FCSTD DOCUMENT  (FreeCAD 1.0R39319 (Git))
Label: OctoForge-A
License: Creative Commons Attribution 4.0
LicenseURL: https://creativecommons.org/licenses/by/4.0/
objects: App::FeaturePython×6, App::LinkElement×4, App::Link×3, App::DocumentObjectGroup×1, Assembly::JointGroup×1, Assembly::AssemblyObject×1
EXTERNAL_REF file=Frame/OCT-FRAME-A.FCStd obj=Assembly
EXTERNAL_REF file=Insulation/OCT-CHMBR-A.FCStd obj=Assembly
EXTERNAL_REF file=Electronics/OCT-HELEM-A.FCStd obj=Part

FEATURE [App::Link] Link  label="OCT-FRAME-A"
  LinkPlacement = pos=(-67.4025,-29.5359,22.5821) rot=(0,0,1;0rad)
  LinkedObject = -> <external Frame/OCT-FRAME-A.FCStd>#Assembly
  Placement = pos=(-67.4025,-29.5359,22.5821) rot=(0,0,1;0rad)
FEATURE [App::FeaturePython] GroundedJoint  # Assembly grounded joint (typed FeaturePython)
  ObjectToGround = -> Link
  Placement = pos=(-67.4025,-29.5359,22.5821) rot=(0,0,1;0rad)
FEATURE [App::Link] Link001  label="OCT-CHMBR-A"
  LinkPlacement = pos=(-67.4025,-29.5359,185.582) rot=(0,0,1;0rad)
  LinkedObject = -> <external Insulation/OCT-CHMBR-A.FCStd>#Assembly
  Placement = pos=(-67.4025,-29.5359,185.582) rot=(0,0,1;0rad)
FEATURE [App::FeaturePython] Joint  label="Fixed"  # Assembly joint (typed FeaturePython)
  Activated = true
  AngleMax = 0
  AngleMin = 0
  Detach1 = false
  Detach2 = false
  Distance = 0
  Distance2 = 0
  EnableAngleMax = false
  EnableAngleMin = false
  EnableLengthMax = false
  EnableLengthMin = false
  JointType = 0 (Fixed)
  LengthMax = 0
  LengthMin = 0
  Offset2 = pos=(0,0,0) rot=(0,0,1;3.14159rad)
  Placement1 = pos=(3.2e-15,111,0) rot=(-0.707107,0,0.707107;3.14159rad)
  Placement2 = pos=(-3.2e-15,0,0) rot=(0,-1,0;4.71239rad)
  Reference1 = -> Assembly [Link001.OCT_CHBRK_BA.Edge21,Link001.OCT_CHBRK_BA.Edge21]
  Reference2 = -> Assembly [Link.brace.Edge5,Link.brace.Edge5]
FEATURE [App::LinkElement] OCT_HELEM_A_i0
  LinkPlacement = pos=(-67.4025,-29.5359,374.582) rot=(0,0,1;0.785398rad)
  LinkedObject = -> <external Electronics/OCT-HELEM-A.FCStd>#Part
  Placement = pos=(-67.4025,-29.5359,374.582) rot=(0,0,1;0.785398rad)
  _LinkOwner = 55
FEATURE [App::LinkElement] OCT_HELEM_A_i1
  LinkPlacement = pos=(-67.4025,-29.5359,341.582) rot=(0,0,1;0.785398rad)
  LinkedObject = -> <external Electronics/OCT-HELEM-A.FCStd>#Part
  Placement = pos=(-67.4025,-29.5359,341.582) rot=(0,0,1;0.785398rad)
  _LinkOwner = 55
FEATURE [App::LinkElement] OCT_HELEM_A_i2
  LinkPlacement = pos=(-67.4025,-29.5359,308.582) rot=(0,0,1;0.785398rad)
  LinkedObject = -> <external Electronics/OCT-HELEM-A.FCStd>#Part
  Placement = pos=(-67.4025,-29.5359,308.582) rot=(0,0,1;0.785398rad)
  _LinkOwner = 55
FEATURE [App::LinkElement] OCT_HELEM_A_i3
  LinkPlacement = pos=(-67.4025,-29.5359,275.582) rot=(0,0,1;0.785398rad)
  LinkedObject = -> <external Electronics/OCT-HELEM-A.FCStd>#Part
  Placement = pos=(-67.4025,-29.5359,275.582) rot=(0,0,1;0.785398rad)
  _LinkOwner = 55
FEATURE [App::Link] OCT_HELEM_A  label="OCT-HELEM-A"
  ElementCount = 4
  ElementList = -> [OCT_HELEM_A_i0,OCT_HELEM_A_i1,OCT_HELEM_A_i2,OCT_HELEM_A_i3]
  LinkedObject = -> <external Electronics/OCT-HELEM-A.FCStd>#Part
FEATURE [App::DocumentObjectGroup] Group  label="Heating Elements"
  Group = -> [OCT_HELEM_A]
FEATURE [App::FeaturePython] Joint001  label="Fixed"  # Assembly joint (typed FeaturePython)
  Activated = true
  AngleMax = 0
  AngleMin = 0
  Detach1 = false
  Detach2 = false
  Distance = 0
  Distance2 = 0
  EnableAngleMax = false
  EnableAngleMin = false
  EnableLengthMax = false
  EnableLengthMin = false
  JointType = 0 (Fixed)
  LengthMax = 0
  LengthMin = 0
  Offset2 = pos=(0,0,0) rot=(0,0,-1;1.5708rad)
  Placement1 = pos=(-3.6e-15,-35,-7.1e-15) rot=(-1,0,0;4.71239rad)
  Placement2 = pos=(1.1e-14,35,189) rot=(0,-0.707107,-0.707107;3.14159rad)
  Reference1 = -> Assembly [OCT_HELEM_A.OCT_HELEM_A_i0.Link.Link_i1.Edge2,OCT_HELEM_A.OCT_HELEM_A_i0.Link.Link_i1.Edge2]
  Reference2 = -> Assembly [Link001.OCT_CHBRK_BA.Edge35,Link001.OCT_CHBRK_BA.Edge35]
FEATURE [App::FeaturePython] Joint002  label="Fixed"  # Assembly joint (typed FeaturePython)
  Activated = true
  AngleMax = 0
  AngleMin = 0
  Detach1 = false
  Detach2 = false
  Distance = 0
  Distance2 = 0
  EnableAngleMax = false
  EnableAngleMin = false
  EnableLengthMax = false
  EnableLengthMin = false
  JointType = 0 (Fixed)
  LengthMax = 0
  LengthMin = 0
  Offset2 = pos=(0,0,0) rot=(0,0,-1;1.5708rad)
  Placement1 = pos=(-3.6e-15,-35,-7.1e-15) rot=(-1,0,0;4.71239rad)
  Placement2 = pos=(7e-15,35,156) rot=(0,-0.707107,-0.707107;3.14159rad)
  Reference1 = -> Assembly [OCT_HELEM_A.OCT_HELEM_A_i1.Link.Link_i1.Edge2,OCT_HELEM_A.OCT_HELEM_A_i1.Link.Link_i1.Edge2]
  Reference2 = -> Assembly [Link001.OCT_CHBRK_BA.Edge49,Link001.OCT_CHBRK_BA.Edge49]
FEATURE [App::FeaturePython] Joint003  label="Fixed"  # Assembly joint (typed FeaturePython)
  Activated = true
  AngleMax = 0
  AngleMin = 0
  Detach1 = false
  Detach2 = false
  Distance = 0
  Distance2 = 0
  EnableAngleMax = false
  EnableAngleMin = false
  EnableLengthMax = false
  EnableLengthMin = false
  JointType = 0 (Fixed)
  LengthMax = 0
  LengthMin = 0
  Offset2 = pos=(0,0,0) rot=(0,0,-1;1.5708rad)
  Placement1 = pos=(-3.6e-15,-35,-7.1e-15) rot=(-1,0,0;4.71239rad)
  Placement2 = pos=(4e-15,35,123) rot=(0,-0.707107,-0.707107;3.14159rad)
  Reference1 = -> Assembly [OCT_HELEM_A.OCT_HELEM_A_i2.Link.Link_i1.Edge2,OCT_HELEM_A.OCT_HELEM_A_i2.Link.Link_i1.Edge2]
  Reference2 = -> Assembly [Link001.OCT_CHBRK_BA.Edge63,Link001.OCT_CHBRK_BA.Edge63]
FEATURE [App::FeaturePython] Joint004  label="Fixed"  # Assembly joint (typed FeaturePython)
  Activated = true
  AngleMax = 0
  AngleMin = 0
  Detach1 = false
  Detach2 = false
  Distance = 0
  Distance2 = 0
  EnableAngleMax = false
  EnableAngleMin = false
  EnableLengthMax = false
  EnableLengthMin = false
  JointType = 0 (Fixed)
  LengthMax = 0
  LengthMin = 0
  Offset2 = pos=(0,0,0) rot=(0,0,-1;1.5708rad)
  Placement1 = pos=(-3.6e-15,-35,-7.1e-15) rot=(-1,0,0;4.71239rad)
  Placement2 = pos=(0,35,90) rot=(0,-0.707107,-0.707107;3.14159rad)
  Reference1 = -> Assembly [OCT_HELEM_A.OCT_HELEM_A_i3.Link.Link_i1.Edge2,OCT_HELEM_A.OCT_HELEM_A_i3.Link.Link_i1.Edge2]
  Reference2 = -> Assembly [Link001.OCT_CHBRK_BA.Edge77,Link001.OCT_CHBRK_BA.Edge77]
FEATURE [Assembly::JointGroup] Joints
  Group = -> [GroundedJoint,Joint,Joint001,Joint002,Joint003,Joint004]
FEATURE [Assembly::AssemblyObject] Assembly  label="OctoForge"
  Group = -> [Joints,Link,GroundedJoint,Link001,Joint,Group,OCT_HELEM_A,Joint001,Joint002,Joint003,Joint004]
  Origin = -> Origin
  Type = Assembly

RESOLVED EXTERNAL PARTS (link-assembly join: the EXTERNAL_REF files above that resolve inside this repo's crawl, each included once):
---- part Electronics/OCT-HELEM-A.FCStd = doc fcstd_b4418c379665 ----
FCSTD DOCUMENT  (FreeCAD 1.0R39319 (Git))
Label: OCT-HELEM-A
License: Creative Commons Attribution 4.0
LicenseURL: https://creativecommons.org/licenses/by/4.0/
objects: Sketcher::SketchObject×9, Part::FeaturePython×9, PartDesign::Plane×3, PartDesign::SubShapeBinder×3, PartDesign::Line×2, PartDesign::Body×2, App::Part×2, App::LinkElement×2, App::VarSet×1, PartDesign::Point×1, PartDesign::AdditivePipe×1, PartDesign::Pad×1, App::Link×1, App::DocumentObjectGroup×1
note: 44 computed .brp shape members not serialized (recipe doc carries the construction recipe); baked Part::Feature solids carry a one-line shape summary decoded from their .brp

FEATURE [App::VarSet] VarSet  label="dims"
  arcAngle = 300
  barLength = 86
  brickThickness = 76
  chamberDiameter = 70
  coilDiameter = 6.02
  dTerminal = 4
  lWire = 866.98
  loopDiameter = 83
  pitch = 4.89634
  wireDiameter = 1.02
  expr: barLength = brickThickness + 10 mm
  expr: pitch = pi * coilDiameter * tan(asin(0.5 * loopDiameter * arcAngle * pi / (180 * lWire * 1 deg)))
FEATURE [Sketcher::SketchObject] Sketch006  label="coil path"
  ArcFitTolerance = 1e-06
  AttachmentSupport = -> [XY_Plane002]
  FullyConstrained = true
  MakeInternals = false
  MapMode = 5
  expr: Constraints[1] = <<dims>>.arcAngle
  expr: Constraints[3] = <<dims>>.loopDiameter / 2
  sketch-geometry (5):
    g0: ArcOfCircle CenterX=0 CenterY=0 CenterZ=0 NormalX=0 NormalY=0 NormalZ=1 AngleXU=0 Radius=41.5 StartAngle=4.84329 EndAngle=10.0793
    g1: LineSegment [constr] StartX=0 StartY=0 StartZ=0 EndX=-15.8814 EndY=-38.341 EndZ=0
    g2: LineSegment [constr] StartX=-32.9242 StartY=-25.2636 StartZ=0 EndX=-15.8814 EndY=-38.341 EndZ=0
    g3: LineSegment [constr] StartX=5.41684 StartY=-41.145 StartZ=0 EndX=-15.8814 EndY=-38.341 EndZ=0
    g4: LineSegment [constr] StartX=0 StartY=0 StartZ=0 EndX=-32.9242 EndY=-25.2636 EndZ=0
  constraints (14):
    c: Coincident(g0,g-1)
    c: Angle(g0) = 5.23599
    c: Coincident(g1,g0)
    c: Radius(g0) = 41.5
    c: PointOnObject(g1,g0)
    c: Coincident(g2,g0)
    c: Coincident(g2,g1)
    c: Coincident(g3,g0)
    c: Coincident(g3,g1)
    c: Equal(g2,g3)
    c: Coincident(g4,g0)
    c: Coincident(g4,g0)
    c: Angle(g-2,g4) = 2.22529
    c: Angle(g-2,g1) = 2.74889
FEATURE [PartDesign::Plane] DatumPlane  label="coil start right"
  AttachmentOffset = pos=(0,0,0) rot=(0,1,0;0.1309rad)
  AttachmentSupport = -> [YZ_Plane003]
  Length = 114.074
  MapMode = 5
  Placement = pos=(0,0,0) rot=(0.527011,0.600941,0.600941;2.17155rad)
  ResizeMode = 0
  Width = 64.1376
  expr: .AttachmentOffset.Rotation.Pitch = -22.5 + (360 - <<dims>>.arcAngle / deg) / 2
FEATURE [Part::FeaturePython] PathHelix  # WARN: FeaturePython — macro-defined, semantics opaque (R4)
  Count = 44.3787
  ExtraHalf = false
  Join = true
  Pitch = 4.89634
  Radius = 3.01
  Resolution = 4
  Reverse = true
  Rotation = 180
  Spine = -> Sketch006
  expr: Pitch = <<dims>>.pitch
  expr: Radius = <<dims>>.coilDiameter / 2
FEATURE [PartDesign::SubShapeBinder] Binder  label="loop binder"
  BindCopyOnChange = 0
  BindMode = 0
  ClaimChildren = false
  Context = -> Part [Part001.Body001.Binder.]
  Fuse = false
  MakeFace = true
  OffsetFill = false
  OffsetIntersection = false
  OffsetJoinType = 0
  OffsetOpenResult = false
  PartialLoad = false
  Relative = true
  Support = -> [Sketch006]
  _Version = 2
FEATURE [Sketcher::SketchObject] Sketch  label="terminal loop right"
  ArcFitTolerance = 1e-06
  AttachmentOffset = pos=(0,0,41.5) rot=(0,0,1;0rad)
  AttachmentSupport = -> [XZ_Plane003]
  FullyConstrained = true
  MakeInternals = false
  MapMode = 5
  Placement = pos=(0,-41.5,9.2e-15) rot=(1,0,0;1.5708rad)
  expr: .AttachmentOffset.Base.z = <<dims>>.loopDiameter / 2
  expr: Constraints[3] = (<<dims>>.dTerminal + <<dims>>.wireDiameter) / 2
  sketch-geometry (2):
    g0: ArcOfCircle CenterX=0 CenterY=0 CenterZ=0 NormalX=0 NormalY=0 NormalZ=1 AngleXU=0 Radius=2.51 StartAngle=0.288902 EndAngle=5.78669
    g1: ArcOfCircle CenterX=3.36454 CenterY=1 CenterZ=0 NormalX=0 NormalY=0 NormalZ=1 AngleXU=0 Radius=1 StartAngle=3.4305 EndAngle=4.71239
  constraints (6):
    c: Coincident(g0,g-1)
    c: Tangent(g0,g1) = 1.5708
    c: Tangent(g1,g-1) = -1.5708
    c: Radius(g0) = 2.51
    c: Radius(g1) = 1
    c: Angle(g0) = 5.49779
FEATURE [Sketcher::SketchObject] Sketch007  label="xy transition right"
  ArcFitTolerance = 1e-06
  AttachmentSupport = -> [XY_Plane003]
  ExternalGeometry = -> [Sketch,Binder]
  FullyConstrained = true
  MakeInternals = false
  MapMode = 5
  sketch-geometry (3):
    g0: ArcOfCircle CenterX=3.36454 CenterY=-40.4973 CenterZ=0 NormalX=0 NormalY=0 NormalZ=1 AngleXU=0 Radius=1.00271 StartAngle=4.71239 EndAngle=5.33537
    g1: ArcOfCircle CenterX=4.53463 CenterY=-42.126 CenterZ=0 NormalX=0 NormalY=0 NormalZ=1 AngleXU=0 Radius=1.00271 StartAngle=0.1309 EndAngle=2.19378
    g2: LineSegment [constr] StartX=5.52876 StartY=-41.9951 StartZ=0 EndX=0 EndY=0 EndZ=0
  constraints (7):
    c: Tangent(g1,g0) = 1.5708
    c: Tangent(g2,g1) = -1.5708
    c: Coincident(g2,g-1)
    c: PointOnObject(g-4,g2)
    c: PointOnObject(g0,g-4)
    c: Tangent(g-3,g0) = -1.5708
    c: Equal(g1,g0)
FEATURE [PartDesign::SubShapeBinder] Binder001  label="coil binder"
  BindCopyOnChange = 0
  BindMode = 0
  ClaimChildren = false
  Context = -> Part [Part001.Body001.Binder001.]
  Fuse = false
  MakeFace = true
  OffsetFill = false
  OffsetIntersection = false
  OffsetJoinType = 0
  OffsetOpenResult = false
  PartialLoad = false
  Relative = true
  Support = -> [PathHelix]
  _Version = 2
FEATURE [Sketcher::SketchObject] Sketch008  label="coil transition right"
  ArcFitTolerance = 1e-06
  AttachmentSupport = -> [DatumPlane]
  ExternalGeometry = -> [Binder001,Sketch007]
  FullyConstrained = true
  MakeInternals = false
  MapMode = 5
  Placement = pos=(0,0,0) rot=(0.527011,0.600941,0.600941;2.17155rad)
  expr: Constraints[1] = <<dims>>.loopDiameter / 2
  expr: Constraints[2] = <<dims>>.coilDiameter
  sketch-geometry (3):
    g0: Circle [constr] CenterX=-41.5 CenterY=0 CenterZ=0 NormalX=0 NormalY=0 NormalZ=1 AngleXU=0 Radius=3.01
    g1: ArcOfCircle CenterX=-42.3575 CenterY=1.38287 CenterZ=0 NormalX=0 NormalY=0 NormalZ=1 AngleXU=0 Radius=1.38287 StartAngle=2.12583 EndAngle=4.71238
    g2: ArcOfCircle CenterX=-41.5 CenterY=0 CenterZ=0 NormalX=0 NormalY=0 NormalZ=1 AngleXU=0 Radius=3.01 StartAngle=1.5708 EndAngle=2.12583
  constraints (8):
    c: PointOnObject(g0,g-1)
    c: DistanceX(g0,g-1) = 41.5
    c: Diameter(g0) = 6.02
    c: Coincident(g1,g-4)
    c: Tangent(g1,g-1)
    c: Coincident(g2,g-3)
    c: Coincident(g2,g0)
    c: Tangent(g1,g2) = -1.5708
FEATURE [Sketcher::SketchObject] Sketch009  label="wire cross section"
  ArcFitTolerance = 1e-06
  AttachmentSupport = -> [YZ_Plane003]
  FullyConstrained = true
  MakeInternals = false
  MapMode = 5
  Placement = pos=(0,0,0) rot=(0.57735,0.57735,0.57735;2.0944rad)
  expr: Constraints[0] = <<dims>>.wireDiameter
  expr: Constraints[1] = <<dims>>.loopDiameter / 2
  expr: Constraints[2] = (<<dims>>.dTerminal + <<dims>>.wireDiameter) / 2
  sketch-geometry (1):
    g0: Circle CenterX=-41.5 CenterY=-2.51 CenterZ=0 NormalX=0 NormalY=0 NormalZ=1 AngleXU=0 Radius=0.51
  constraints (3):
    c: Diameter(g0) = 1.02
    c: DistanceX(g0,g-1) = 41.5
    c: DistanceY(g0,g-1) = 2.51
FEATURE [PartDesign::Line] DatumLine  label="terminal axis left"
  AttacherType = Attacher::AttachEngineLine
  AttachmentOffset = pos=(0,0,0) rot=(0,-1,0;0.785398rad)
  AttachmentSupport = -> [Y_Axis003]
  Length = 20
  MapMode = 29
  Placement = pos=(0,0,0) rot=(0.281085,0.678598,0.678598;2.59356rad)
  ResizeMode = 0
FEATURE [PartDesign::Plane] DatumPlane001  label="terminal left plane"
  AttachmentOffset = pos=(0,0,41.5) rot=(0,0,1;0rad)
  AttachmentSupport = -> [DatumLine]
  Length = 142.427
  MapMode = 7
  Placement = pos=(-29.3449,-29.3449,0) rot=(0.862856,-0.357407,-0.357407;1.71777rad)
  ResizeMode = 0
  Width = 65.9072
  expr: .AttachmentOffset.Base.z = <<dims>>.loopDiameter / 2
FEATURE [Sketcher::SketchObject] Sketch010  label="terminal loop left"
  ArcFitTolerance = 1e-06
  AttachmentSupport = -> [DatumPlane001]
  FullyConstrained = true
  MakeInternals = false
  MapMode = 5
  Placement = pos=(-29.3449,-29.3449,0) rot=(0.862856,-0.357407,-0.357407;1.71777rad)
  expr: Constraints[1] = (<<dims>>.dTerminal + <<dims>>.wireDiameter) / 2
  sketch-geometry (2):
    g0: ArcOfCircle CenterX=0 CenterY=0 CenterZ=0 NormalX=0 NormalY=0 NormalZ=1 AngleXU=0 Radius=2.51 StartAngle=3.63809 EndAngle=9.13588
    g1: ArcOfCircle CenterX=-3.36454 CenterY=1 CenterZ=0 NormalX=0 NormalY=0 NormalZ=1 AngleXU=0 Radius=1 StartAngle=4.71239 EndAngle=5.99428
  constraints (6):
    c: Coincident(g0,g-1)
    c: Radius(g0) = 2.51
    c: Radius(g1) = 1
    c: Tangent(g1,g0) = 1.5708
    c: Tangent(g1,g-1) = -1.5708
    c: Angle(g0) = 5.49779
FEATURE [PartDesign::Point] DatumPoint  label="coil start point left"
  AttacherType = Attacher::AttachEnginePoint
  AttachmentSupport = -> [Binder001]
  MapMode = 37
  Placement = pos=(-34.0198,-23.7677,3.01) rot=(0,0,1;0rad)
FEATURE [PartDesign::Plane] DatumPlane002  label="coil start plane left"
  AttachmentSupport = -> [Binder001,Z_Axis003]
  Length = 140.493
  MapMode = 13
  Placement = pos=(-11.3399,-7.92258,1.33667) rot=(0.913595,0.287528,0.287528;1.66104rad)
  ResizeMode = 0
  Width = 65.7925
FEATURE [Sketcher::SketchObject] Sketch011  label="xy transition left"
  ArcFitTolerance = 1e-06
  AttachmentSupport = -> [XY_Plane003]
  ExternalGeometry = -> [Sketch010,Binder001]
  FullyConstrained = true
  MakeInternals = false
  MapMode = 5
  expr: Constraints[4] = <<dims>>.loopDiameter / 2
  sketch-geometry (4):
    g0: ArcOfCircle CenterX=-24.9661 CenterY=-20.2079 CenterZ=0 NormalX=0 NormalY=0 NormalZ=1 AngleXU=0 Radius=9.55715 StartAngle=3.60279 EndAngle=3.92699
    g1: ArcOfCircle CenterX=-32.6292 CenterY=-24.0161 CenterZ=0 NormalX=0 NormalY=0 NormalZ=1 AngleXU=0 Radius=1 StartAngle=2.18061 EndAngle=3.60279
    g2: LineSegment [constr] StartX=-33.5247 StartY=-24.4611 StartZ=0 EndX=0 EndY=3.6e-15 EndZ=0
    g3: LineSegment [constr] StartX=-34.0198 StartY=-23.7677 StartZ=0 EndX=0 EndY=0 EndZ=0
  constraints (9):
    c: Tangent(g0,g-3) = -1.5708
    c: Tangent(g0,g1) = -1.5708
    c: Coincident(g2,g0)
    c: Coincident(g2,g-1)
    c: Distance(g2,g2) = 41.5
    c: Coincident(g3,g-4)
    c: Coincident(g3,g2)
    c: Tangent(g1,g3) = 1.5708
    c: Radius(g1) = 1
FEATURE [Sketcher::SketchObject] Sketch012  label="coil transition left"
  ArcFitTolerance = 1e-06
  AttachmentSupport = -> [DatumPlane002]
  ExternalGeometry = -> [Sketch011,DatumPoint]
  FullyConstrained = true
  MakeInternals = false
  MapMode = 5
  Placement = pos=(-11.3399,-7.92258,1.33667) rot=(0.913595,0.287528,0.287528;1.66104rad)
  sketch-geometry (3):
    g0: Circle [constr] CenterX=-27.6579 CenterY=-1.33667 CenterZ=0 NormalX=0 NormalY=0 NormalZ=1 AngleXU=0 Radius=3.01001
    g1: ArcOfCircle CenterX=-26.6689 CenterY=0.00586924 CenterZ=0 NormalX=0 NormalY=0 NormalZ=1 AngleXU=0 Radius=1.34254 StartAngle=4.71239 EndAngle=7.21908
    g2: ArcOfCircle CenterX=-27.6579 CenterY=-1.33667 CenterZ=0 NormalX=0 NormalY=0 NormalZ=1 AngleXU=0 Radius=3.01001 StartAngle=0.935895 EndAngle=1.5737
  constraints (6):
    c: Coincident(g0,g-3)
    c: PointOnObject(g1,g0)
    c: Coincident(g2,g0)
    c: Tangent(g2,g1) = -1.5708
    c: Tangent(g1,g-3) = 1.5708
    c: Coincident(g2,g-4)
FEATURE [PartDesign::SubShapeBinder] Binder002  label="full path binder"
  BindCopyOnChange = 0
  BindMode = 0
  ClaimChildren = false
  Context = -> Part [Part001.Body001.Binder002.]
  Fuse = false
  MakeFace = true
  OffsetFill = false
  OffsetIntersection = false
  OffsetJoinType = 0
  OffsetOpenResult = false
  PartialLoad = false
  Refine = true
  Relative = true
  Support = -> [Sketch007,Sketch,Sketch011,Sketch008,Sketch010,Sketch012,Binder001]
  _Version = 2
FEATURE [PartDesign::AdditivePipe] AdditivePipe
  AuxilleryCurvelinear = true
  AuxillerySpineTangent = false
  Binormal = (0,0,0)
  Mode = 0
  Placement = pos=(0,0,0) rot=(1,1,1;2.0944rad)
  Profile = -> Sketch009
  Refine = true
  Spine = -> Binder002
  SpineTangent = false
  Suppressed = false
  Transformation = 0
  Transition = 0
FEATURE [PartDesign::Line] DatumLine001  label="terminal axis right"
  AttacherType = Attacher::AttachEngineLine
  AttachmentSupport = -> [Y_Axis003]
  Length = 20
  MapMode = 29
  Placement = pos=(0,0,0) rot=(0,0.707107,0.707107;3.14159rad)
  ResizeMode = 0
FEATURE [PartDesign::Body] Body001  label="element body"
  AllowCompound = false
  Group = -> [DatumPlane,DatumLine001,DatumPlane001,DatumLine,Binder,Binder001,DatumPoint,DatumPlane002,Sketch,Sketch007,Sketch008,Sketch009,Sketch010,Sketch011,Sketch012,Binder002,AdditivePipe]
  Origin = -> Origin003
  Tip = -> AdditivePipe
FEATURE [App::Part] Part001  label="OCT-HWIRE-AA"
  Group = -> [Sketch006,Body001,PathHelix]
  Origin = -> Origin002
FEATURE [Sketcher::SketchObject] Sketch013
  ArcFitTolerance = 1e-06
  AttachmentOffset = pos=(0,0,35) rot=(0,0,1;0rad)
  AttachmentSupport = -> [XZ_Plane]
  FullyConstrained = true
  MakeInternals = false
  MapMode = 5
  Placement = pos=(0,-35,7.8e-15) rot=(1,0,0;1.5708rad)
  expr: .AttachmentOffset.Base.z = <<dims>>.chamberDiameter / 2
  expr: Constraints[1] = <<dims>>.dTerminal
  sketch-geometry (1):
    g0: Circle CenterX=0 CenterY=0 CenterZ=0 NormalX=0 NormalY=0 NormalZ=1 AngleXU=0 Radius=2
  constraints (2):
    c: Coincident(g0,g-1)
    c: Diameter(g0) = 4
FEATURE [PartDesign::Pad] Pad
  Direction = (0,-1,2e-16)
  Length = 86
  Length2 = 10
  Placement = pos=(0,0,0) rot=(1,0,0;1.5708rad)
  Profile = -> Sketch013
  ReferenceAxis = -> Sketch013 [N_Axis]
  Refine = true
  Suppressed = false
  Type = 0
  expr: Length = <<dims>>.barLength
FEATURE [PartDesign::Body] Body  label="OCT-PWBAR-AA"
  AllowCompound = false
  Group = -> [Sketch013,Pad]
  Origin = -> Origin
  Tip = -> Pad
FEATURE [App::LinkElement] Link_i0
  LinkedObject = -> Body
  _LinkOwner = 2349
FEATURE [App::LinkElement] Link_i1
  LinkPlacement = pos=(0,0,0) rot=(0,0,1;-0.785398rad)
  LinkedObject = -> Body
  Placement = pos=(0,0,0) rot=(0,0,1;-0.785398rad)
  _LinkOwner = 2349
FEATURE [App::Link] Link  label="OCT-PWBAR-AA"
  ElementCount = 2
  ElementList = -> [Link_i0,Link_i1]
  LinkedObject = -> Body
FEATURE [Part::FeaturePython] Nut  label="M4-Nut"  # WARN: FeaturePython — macro-defined, semantics opaque (R4)
  BaseObject = -> Link [Link_i0.Pad.Edge2]
  Diameter = 6
  Invert = true
  LeftHanded = false
  MatchOuter = false
  Offset = -5.99
  OffsetAngle = 0
  Placement = pos=(0,-40.99,9.1e-15) rot=(-1,0,0;1.5708rad)
  Thread = false
  Type = 31
  expr: Offset = (<<dims>>.chamberDiameter - <<dims>>.loopDiameter + <<dims>>.wireDiameter) / 2
FEATURE [Part::FeaturePython] Nut001  label="M4-Nut"  # WARN: FeaturePython — macro-defined, semantics opaque (R4)
  BaseObject = -> Nut [Edge27]
  Diameter = 6
  Invert = true
  LeftHanded = false
  MatchOuter = false
  Offset = 1.02
  OffsetAngle = 0
  Placement = pos=(0,-42.01,9.3e-15) rot=(1,0,0;1.5708rad)
  Thread = false
  Type = 31
  expr: Offset = <<dims>>.wireDiameter
FEATURE [Part::FeaturePython] Nut002  label="M4-Nut"  # WARN: FeaturePython — macro-defined, semantics opaque (R4)
  BaseObject = -> Link [Link_i0.Pad.Edge3]
  Diameter = 6
  Invert = false
  LeftHanded = false
  MatchOuter = true
  Offset = -10
  OffsetAngle = 0
  Placement = pos=(0,-111,2.46e-14) rot=(1,0,0;1.5708rad)
  Thread = false
  Type = 31
  expr: Offset = -(<<dims>>.barLength - <<dims>>.brickThickness)
FEATURE [Part::FeaturePython] Nut003  label="M4-Nut"  # WARN: FeaturePython — macro-defined, semantics opaque (R4)
  BaseObject = -> Nut002 [Edge2]
  Diameter = 6
  Invert = false
  LeftHanded = false
  MatchOuter = true
  Offset = 1
  OffsetAngle = 0
  Placement = pos=(0,-115.2,2.56e-14) rot=(1,0,0;1.5708rad)
  Thread = false
  Type = 31
FEATURE [Part::FeaturePython] Nut004  label="M4-Nut"  # WARN: FeaturePython — macro-defined, semantics opaque (R4)
  BaseObject = -> Link [Link_i1.Pad.Edge2]
  Diameter = 6
  Invert = true
  LeftHanded = false
  MatchOuter = true
  Offset = -5.99
  OffsetAngle = 0
  Placement = pos=(-28.9843,-28.9843,1.55e-14) rot=(-0.707107,0.707107,0;1.5708rad)
  Thread = false
  Type = 31
  expr: Offset = (<<dims>>.chamberDiameter - <<dims>>.loopDiameter + <<dims>>.wireDiameter) / 2
FEATURE [Part::FeaturePython] Nut005  label="M4-Nut"  # WARN: FeaturePython — macro-defined, semantics opaque (R4)
  BaseObject = -> Nut004 [Edge50]
  Diameter = 6
  Invert = true
  LeftHanded = false
  MatchOuter = true
  Offset = 1.02
  OffsetAngle = 0
  Placement = pos=(-29.7056,-29.7056,1.57e-14) rot=(0.707107,-0.707107,0;1.5708rad)
  Thread = false
  Type = 31
  expr: Offset = <<dims>>.wireDiameter
FEATURE [Part::FeaturePython] Nut006  label="M4-Nut"  # WARN: FeaturePython — macro-defined, semantics opaque (R4)
  BaseObject = -> Link [Link_i1.Pad.Edge3]
  Diameter = 6
  Invert = false
  LeftHanded = false
  MatchOuter = true
  Offset = -10
  OffsetAngle = 0
  Placement = pos=(-78.4889,-78.4889,2.62e-14) rot=(0.707107,-0.707107,0;1.5708rad)
  Thread = false
  Type = 31
  expr: Offset = -(<<dims>>.barLength - <<dims>>.brickThickness)
FEATURE [Part::FeaturePython] Nut007  label="M4-Nut"  # WARN: FeaturePython — macro-defined, semantics opaque (R4)
  BaseObject = -> Nut006 [Edge2]
  Diameter = 6
  Invert = false
  LeftHanded = false
  MatchOuter = true
  Offset = 1
  OffsetAngle = 0
  Placement = pos=(-81.4587,-81.4587,2.67e-14) rot=(0.707107,-0.707107,0;1.5708rad)
  Thread = false
  Type = 31
FEATURE [App::DocumentObjectGroup] Group  label="Nuts"
  Group = -> [Nut,Nut001,Nut002,Nut003,Nut004,Nut005,Nut007,Nut006]
FEATURE [App::Part] Part  label="OCT-HELEM-A"
  Group = -> [Part001,Body,Link,Nut001,Nut,Group,Nut002,Nut003,Nut004,Nut005,Nut007,Nut006]
  Origin = -> Origin004
---- part Frame/OCT-FRAME-A.FCStd = doc fcstd_5179656cb496 (128865 chars; too large to inline — full recipe in that document) ----
---- part Insulation/OCT-CHMBR-A.FCStd = doc fcstd_60e0298b71d7 ----
FCSTD DOCUMENT  (FreeCAD 1.0R39319 (Git))
Label: OCT-CHMBR-A
License: Creative Commons Attribution 4.0
LicenseURL: https://creativecommons.org/licenses/by/4.0/
objects: App::Link×9, App::FeaturePython×9, Sketcher::SketchObject×4, PartDesign::Body×3, PartDesign::Pad×2, PartDesign::LinearPattern×2, App::VarSet×1, PartDesign::Pocket×1, PartDesign::FeatureBase×1, PartDesign::Groove×1, Assembly::JointGroup×1, Assembly::AssemblyObject×1
note: 29 computed .brp shape members not serialized (recipe doc carries the construction recipe); baked Part::Feature solids carry a one-line shape summary decoded from their .brp

FEATURE [Sketcher::SketchObject] Sketch
  ArcFitTolerance = 1e-06
  AttachmentSupport = -> [XY_Plane]
  FullyConstrained = true
  MakeInternals = false
  MapMode = 5
  expr: Constraints[53] = <<dims>>.brickDepth
  expr: Constraints[55] = <<dims>>.chamberDiameter
  sketch-geometry (20):
    g0: LineSegment StartX=45.9777 StartY=111 StartZ=0 EndX=-45.9777 EndY=111 EndZ=0
    g1: LineSegment [constr] StartX=-45.9777 StartY=111 StartZ=0 EndX=-111 EndY=45.9777 EndZ=0
    g2: LineSegment [constr] StartX=-111 StartY=45.9777 StartZ=0 EndX=-111 EndY=-45.9777 EndZ=0
    g3: LineSegment [constr] StartX=-111 StartY=-45.9777 StartZ=0 EndX=-45.9777 EndY=-111 EndZ=0
    g4: LineSegment [constr] StartX=-45.9777 StartY=-111 StartZ=0 EndX=45.9777 EndY=-111 EndZ=0
    g5: LineSegment [constr] StartX=45.9777 StartY=-111 StartZ=0 EndX=111 EndY=-45.9777 EndZ=0
    g6: LineSegment [constr] StartX=111 StartY=-45.9777 StartZ=0 EndX=111 EndY=45.9777 EndZ=0
    g7: LineSegment [constr] StartX=111 StartY=45.9777 StartZ=0 EndX=45.9777 EndY=111 EndZ=0
    g8: Circle [constr] CenterX=0 CenterY=0 CenterZ=0 NormalX=0 NormalY=0 NormalZ=1 AngleXU=0 Radius=120.146
    g9: LineSegment [constr] StartX=-14.4975 StartY=35 StartZ=0 EndX=-35 EndY=14.4975 EndZ=0
    g10: LineSegment [constr] StartX=-35 StartY=14.4975 StartZ=0 EndX=-35 EndY=-14.4975 EndZ=0
    g11: LineSegment [constr] StartX=-35 StartY=-14.4975 StartZ=0 EndX=-14.4975 EndY=-35 EndZ=0
    g12: LineSegment [constr] StartX=-14.4975 StartY=-35 StartZ=0 EndX=14.4975 EndY=-35 EndZ=0
    g13: LineSegment [constr] StartX=14.4975 StartY=-35 StartZ=0 EndX=35 EndY=-14.4975 EndZ=0
    g14: LineSegment [constr] StartX=35 StartY=-14.4975 StartZ=0 EndX=35 EndY=14.4975 EndZ=0
    g15: LineSegment [constr] StartX=35 StartY=14.4975 StartZ=0 EndX=14.4975 EndY=35 EndZ=0
    g16: LineSegment StartX=14.4975 StartY=35 StartZ=0 EndX=-14.4975 EndY=35 EndZ=0
    g17: Circle [constr] CenterX=0 CenterY=0 CenterZ=0 NormalX=0 NormalY=0 NormalZ=1 AngleXU=0 Radius=37.8837
    g18: LineSegment StartX=-45.9777 StartY=111 StartZ=0 EndX=-14.4975 EndY=35 EndZ=0
    g19: LineSegment StartX=14.4975 StartY=35 StartZ=0 EndX=45.9777 EndY=111 EndZ=0
  constraints (44):
    c: Coincident(g0,g1)
    c: Coincident(g1,g2)
    c: Coincident(g2,g3)
    c: Coincident(g3,g4)
    c: Coincident(g4,g5)
    c: Coincident(g5,g6)
    c: Coincident(g6,g7)
    c: Coincident(g7,g0)
    c: Equal(g0, g1-g7) x7
    c: PointOnObject(g0,g8)
    c: PointOnObject(g1,g8)
    c: PointOnObject(g2,g8)
    c: PointOnObject(g3,g8)
    c: PointOnObject(g4,g8)
    c: PointOnObject(g5,g8)
    c: PointOnObject(g6,g8)
    c: PointOnObject(g7,g8)
    c: Coincident(g8,g-1)
    c: Horizontal(g0)
    c: Coincident(g9,g10)
    c: Coincident(g10,g11)
    c: Coincident(g11,g12)
    c: Coincident(g12,g13)
    c: Coincident(g13,g14)
    c: Coincident(g14,g15)
    c: Coincident(g15,g16)
    c: Coincident(g16,g9)
    c: Equal(g9, g10-g16) x7
    c: PointOnObject(g9,g17)
    c: PointOnObject(g10,g17)
    c: PointOnObject(g11,g17)
    c: PointOnObject(g12,g17)
    c: PointOnObject(g13,g17)
    c: PointOnObject(g14,g17)
    c: PointOnObject(g15,g17)
    c: PointOnObject(g16,g17)
    c: Coincident(g17,g8)
    c: Coincident(g18,g0)
    c: Coincident(g18,g9)
    c: Coincident(g19,g15)
    c: Coincident(g19,g0)
    c: DistanceY(g9,g0) = 76
    c: Horizontal(g16)
    c: DistanceY(g11,g9) = 70
FEATURE [App::VarSet] VarSet  label="dims"
  barDiameter = 4
  baseHeight = 76
  bottomGrooveHeight = 90
  brickDepth = 76
  brickHeight = 226
  chamberDiameter = 70
  coilOD = 7.04
  elementCount = 4
  elementSpacing = 33
  heaterWireDiameter = 1.02
  loopDiameter = 83
  nutThickness = 4
FEATURE [PartDesign::Pad] Pad
  Direction = (0,0,1)
  Length = 226
  Length2 = 10
  Profile = -> Sketch
  ReferenceAxis = -> Sketch [N_Axis]
  Suppressed = false
  Type = 0
  expr: Length = <<dims>>.brickHeight
FEATURE [Sketcher::SketchObject] Sketch001
  ArcFitTolerance = 1e-06
  AttachmentSupport = -> [YZ_Plane]
  FullyConstrained = true
  MakeInternals = false
  MapMode = 5
  Placement = pos=(0,0,0) rot=(0.57735,0.57735,0.57735;2.0944rad)
  expr: Constraints[6] = <<dims>>.loopDiameter / 2
  expr: Constraints[7] = <<dims>>.bottomGrooveHeight
  expr: Constraints[8] = <<dims>>.coilOD
  sketch-geometry (4):
    g0: ArcOfCircle CenterX=0 CenterY=90 CenterZ=0 NormalX=0 NormalY=0 NormalZ=1 AngleXU=0 Radius=3.52 StartAngle=1.5708 EndAngle=4.71239
    g1: ArcOfCircle CenterX=41.5 CenterY=90 CenterZ=0 NormalX=0 NormalY=0 NormalZ=1 AngleXU=0 Radius=3.52 StartAngle=4.71239 EndAngle=7.85398
    g2: LineSegment StartX=2e-16 StartY=93.52 StartZ=0 EndX=41.5 EndY=93.52 EndZ=0
    g3: LineSegment StartX=-6e-16 StartY=86.48 StartZ=0 EndX=41.5 EndY=86.48 EndZ=0
  constraints (10):
    c: Tangent(g0,g2) = 1.5708
    c: Tangent(g0,g3) = -1.5708
    c: Tangent(g1,g2) = 1.5708
    c: Tangent(g1,g3) = -1.5708
    c: Equal(g0,g1)
    c: Horizontal(g2)
    c: DistanceX(g-1,g1) = 41.5
    c: DistanceY(g-1,g1) = 90
    c: DistanceY(g0,g0) = 7.04
    c: PointOnObject(g0,g-2)
FEATURE [PartDesign::Pocket] Pocket  label="element groove"
  BaseFeature = -> Pad
  Direction = (-1,0,0)
  Length = 5
  Length2 = 5
  Midplane = true
  Profile = -> Sketch001
  ReferenceAxis = -> Sketch001 [N_Axis]
  Suppressed = false
  Type = 1
FEATURE [PartDesign::LinearPattern] LinearPattern
  BaseFeature = -> Pocket
  Direction = -> Z_Axis
  Length = 99
  Mode = 1
  Occurrences = 4
  Offset = 33
  Originals = -> [Pocket]
  Suppressed = false
  TransformMode = 0
  expr: Occurrences = <<dims>>.elementCount
  expr: Offset = <<dims>>.elementSpacing
FEATURE [PartDesign::Body] Body  label="OCT-CHBRK-AA"
  AllowCompound = false
  Group = -> [Sketch,Pad,Sketch001,Pocket,LinearPattern]
  Origin = -> Origin
  Tip = -> LinearPattern
FEATURE [PartDesign::FeatureBase] Clone
  BaseFeature = -> Body
  Suppressed = false
FEATURE [Sketcher::SketchObject] Sketch002
  ArcFitTolerance = 1e-06
  AttachmentSupport = -> [YZ_Plane001]
  FullyConstrained = true
  MakeInternals = false
  MapMode = 5
  Placement = pos=(0,0,0) rot=(0.57735,0.57735,0.57735;2.0944rad)
  expr: Constraints[12] = <<dims>>.chamberDiameter / 2
  expr: Constraints[14] = <<dims>>.barDiameter / 2
  expr: Constraints[15] = <<dims>>.heaterWireDiameter + 2 * <<dims>>.nutThickness + 2 mm
  expr: Constraints[16] = <<dims>>.bottomGrooveHeight
  expr: Constraints[17] = <<dims>>.brickDepth
  sketch-geometry (6):
    g0: LineSegment StartX=35 StartY=90 StartZ=0 EndX=111 EndY=90 EndZ=0
    g1: LineSegment StartX=111 StartY=90 StartZ=0 EndX=111 EndY=92 EndZ=0
    g2: LineSegment StartX=111 StartY=92 StartZ=0 EndX=46.02 EndY=92 EndZ=0
    g3: LineSegment StartX=46.02 StartY=92 StartZ=0 EndX=46.02 EndY=95 EndZ=0
    g4: LineSegment StartX=46.02 StartY=95 StartZ=0 EndX=35 EndY=95 EndZ=0
    g5: LineSegment StartX=35 StartY=95 StartZ=0 EndX=35 EndY=90 EndZ=0
  constraints (18):
    c: Horizontal(g0)
    c: Coincident(g0,g1)
    c: Coincident(g1,g2)
    c: Horizontal(g2)
    c: Coincident(g2,g3)
    c: Coincident(g3,g4)
    c: Horizontal(g4)
    c: Coincident(g4,g5)
    c: Coincident(g5,g0)
    c: Vertical(g1)
    c: Vertical(g3)
    c: Vertical(g5)
    c: DistanceX(g-1,g0) = 35
    c: DistanceY(g5,g5) = 5
    c: DistanceY(g1,g1) = 2
    c: DistanceX(g4,g4) = 11.02
    c: DistanceY(g-1,g0) = 90
    c: DistanceX(g4,g1) = 76
FEATURE [PartDesign::Groove] Groove
  Angle = 360
  Angle2 = 60
  Axis = (0,1,0)
  Base = (0,35,90)
  BaseFeature = -> Clone
  Profile = -> Sketch002
  ReferenceAxis = -> Sketch002 [Edge1]
  Suppressed = false
  Type = 0
FEATURE [PartDesign::LinearPattern] LinearPattern001
  BaseFeature = -> Groove
  Direction = -> Z_Axis001
  Length = 99
  Mode = 1
  Occurrences = 4
  Offset = 33
  Originals = -> [Groove]
  Suppressed = false
  TransformMode = 0
  expr: Occurrences = <<dims>>.elementCount
  expr: Offset = <<dims>>.elementSpacing
FEATURE [PartDesign::Body] Body001  label="OCT-CHBRK-BA"
  AllowCompound = false
  Group = -> [Clone,Sketch002,Groove,LinearPattern001]
  Origin = -> Origin001
  Tip = -> LinearPattern001
FEATURE [Sketcher::SketchObject] Sketch003
  ArcFitTolerance = 1e-06
  AttachmentSupport = -> [XY_Plane002]
  FullyConstrained = true
  MakeInternals = false
  MapMode = 5
  expr: Constraints[25] = <<dims>>.chamberDiameter
  sketch-geometry (9):
    g0: LineSegment StartX=-14.4975 StartY=35 StartZ=0 EndX=-35 EndY=14.4975 EndZ=0
    g1: LineSegment StartX=-35 StartY=14.4975 StartZ=0 EndX=-35 EndY=-14.4975 EndZ=0
    g2: LineSegment StartX=-35 StartY=-14.4975 StartZ=0 EndX=-14.4975 EndY=-35 EndZ=0
    g3: LineSegment StartX=-14.4975 StartY=-35 StartZ=0 EndX=14.4975 EndY=-35 EndZ=0
    g4: LineSegment StartX=14.4975 StartY=-35 StartZ=0 EndX=35 EndY=-14.4975 EndZ=0
    g5: LineSegment StartX=35 StartY=-14.4975 StartZ=0 EndX=35 EndY=14.4975 EndZ=0
    g6: LineSegment StartX=35 StartY=14.4975 StartZ=0 EndX=14.4975 EndY=35 EndZ=0
    g7: LineSegment StartX=14.4975 StartY=35 StartZ=0 EndX=-14.4975 EndY=35 EndZ=0
    g8: Circle [constr] CenterX=0 CenterY=0 CenterZ=0 NormalX=0 NormalY=0 NormalZ=1 AngleXU=0 Radius=37.8837
  constraints (20):
    c: Coincident(g0,g1)
    c: Coincident(g1,g2)
    c: Coincident(g2,g3)
    c: Coincident(g3,g4)
    c: Coincident(g4,g5)
    c: Coincident(g5,g6)
    c: Coincident(g6,g7)
    c: Coincident(g7,g0)
    c: Equal(g0, g1-g7) x7
    c: PointOnObject(g0,g8)
    c: PointOnObject(g1,g8)
    c: PointOnObject(g2,g8)
    c: PointOnObject(g3,g8)
    c: PointOnObject(g4,g8)
    c: PointOnObject(g5,g8)
    c: PointOnObject(g6,g8)
    c: PointOnObject(g7,g8)
    c: Coincident(g8,g-1)
    c: Horizontal(g7)
    c: DistanceY(g2,g0) = 70
FEATURE [PartDesign::Pad] Pad001
  Direction = (0,0,1)
  Length = 76
  Length2 = 10
  Profile = -> Sketch003
  ReferenceAxis = -> Sketch003 [N_Axis]
  Suppressed = false
  Type = 0
  expr: Length = <<dims>>.baseHeight
FEATURE [PartDesign::Body] Body002  label="OCT-CHBRK-CA"
  AllowCompound = false
  Group = -> [Sketch003,Pad001]
  Origin = -> Origin002
  Tip = -> Pad001
FEATURE [App::Link] OCT_CHBRK_CA  label="OCT-CHBRK-CA"
  LinkedObject = -> Body002
FEATURE [App::FeaturePython] GroundedJoint  # Assembly grounded joint (typed FeaturePython)
  ObjectToGround = -> OCT_CHBRK_CA
FEATURE [App::Link] OCT_CHBRK_AA  label="OCT-CHBRK-AA"
  LinkPlacement = pos=(-1.44e-14,4.8e-15,0) rot=(0,0,1;4.71239rad)
  LinkedObject = -> Body
  Placement = pos=(-1.44e-14,4.8e-15,0) rot=(0,0,1;4.71239rad)
FEATURE [App::Link] OCT_CHBRK_AA001  label="OCT-CHBRK-AA"
  LinkPlacement = pos=(-2.13e-14,-5.3e-15,0) rot=(0,0,-1;0.785398rad)
  LinkedObject = -> Body
  Placement = pos=(-2.13e-14,-5.3e-15,0) rot=(0,0,-1;0.785398rad)
FEATURE [App::Link] OCT_CHBRK_AA002  label="OCT-CHBRK-AA"
  LinkPlacement = pos=(5.3e-15,-1.42e-14,0) rot=(0,0,1;0rad)
  LinkedObject = -> Body
  Placement = pos=(5.3e-15,-1.42e-14,0) rot=(0,0,1;0rad)
FEATURE [App::Link] OCT_CHBRK_AA003  label="OCT-CHBRK-AA"
  LinkPlacement = pos=(3.55e-14,7.1e-15,0) rot=(0,0,1;0.785398rad)
  LinkedObject = -> Body
  Placement = pos=(3.55e-14,7.1e-15,0) rot=(0,0,1;0.785398rad)
FEATURE [App::Link] OCT_CHBRK_AA004  label="OCT-CHBRK-AA"
  LinkPlacement = pos=(2.78e-14,1.91e-14,0) rot=(0,0,1;1.5708rad)
  LinkedObject = -> Body
  Placement = pos=(2.78e-14,1.91e-14,0) rot=(0,0,1;1.5708rad)
FEATURE [App::Link] OCT_CHBRK_AA005  label="OCT-CHBRK-AA"
  LinkPlacement = pos=(1.42e-14,2.84e-14,0) rot=(0,0,1;2.35619rad)
  LinkedObject = -> Body
  Placement = pos=(1.42e-14,2.84e-14,0) rot=(0,0,1;2.35619rad)
FEATURE [App::Link] OCT_CHBRK_BA  label="OCT-CHBRK-BA"
  LinkPlacement = pos=(-2.94e-14,2.84e-14,0) rot=(0,0,1;3.14159rad)
  LinkedObject = -> Body001
  Placement = pos=(-2.94e-14,2.84e-14,0) rot=(0,0,1;3.14159rad)
FEATURE [App::Link] OCT_CHBRK_BA001  label="OCT-CHBRK-BA"
  LinkPlacement = pos=(-2.52e-14,5.3e-15,0) rot=(0,0,1;3.92699rad)
  LinkedObject = -> Body001
  Placement = pos=(-2.52e-14,5.3e-15,0) rot=(0,0,1;3.92699rad)
FEATURE [App::FeaturePython] Joint  label="Fixed"  # Assembly joint (typed FeaturePython)
  Activated = true
  AngleMax = 0
  AngleMin = 0
  Detach1 = false
  Detach2 = false
  Distance = 0
  Distance2 = 0
  EnableAngleMax = false
  EnableAngleMin = false
  EnableLengthMax = false
  EnableLengthMin = false
  JointType = 0 (Fixed)
  LengthMax = 0
  LengthMin = 0
  Offset2 = pos=(0,0,0) rot=(0,0,1;3.14159rad)
  Placement1 = pos=(-14.4975,-35,0) rot=(0,0,1;0rad)
  Placement2 = pos=(14.4975,35,0) rot=(0,0,1;3.14159rad)
  Reference1 = -> Assembly [OCT_CHBRK_CA.Edge8,OCT_CHBRK_CA.Vertex7]
  Reference2 = -> Assembly [OCT_CHBRK_BA.Edge20,OCT_CHBRK_BA.Vertex1]
FEATURE [App::FeaturePython] Joint001  label="Fixed"  # Assembly joint (typed FeaturePython)
  Activated = true
  AngleMax = 0
  AngleMin = 0
  Detach1 = false
  Detach2 = false
  Distance = 0
  Distance2 = 0
  EnableAngleMax = false
  EnableAngleMin = false
  EnableLengthMax = false
  EnableLengthMin = false
  JointType = 0 (Fixed)
  LengthMax = 0
  LengthMin = 0
  Offset2 = pos=(0,0,0) rot=(0,0,1;2.35619rad)
  Placement1 = pos=(14.4975,-35,0) rot=(0,0,1;0rad)
  Placement2 = pos=(14.4975,35,0) rot=(0,0,1;2.35619rad)
  Reference1 = -> Assembly [OCT_CHBRK_CA.Edge11,OCT_CHBRK_CA.Vertex9]
  Reference2 = -> Assembly [OCT_CHBRK_BA001.Edge20,OCT_CHBRK_BA001.Vertex1]
FEATURE [App::FeaturePython] Joint002  label="Fixed"  # Assembly joint (typed FeaturePython)
  Activated = true
  AngleMax = 0
  AngleMin = 0
  Detach1 = false
  Detach2 = false
  Distance = 0
  Distance2 = 0
  EnableAngleMax = false
  EnableAngleMin = false
  EnableLengthMax = false
  EnableLengthMin = false
  JointType = 0 (Fixed)
  LengthMax = 0
  LengthMin = 0
  Offset2 = pos=(0,0,0) rot=(0,0,1;1.5708rad)
  Placement1 = pos=(35,-14.4975,0) rot=(0,0,1;0rad)
  Placement2 = pos=(14.4975,35,0) rot=(0,0,1;1.5708rad)
  Reference1 = -> Assembly [OCT_CHBRK_CA.Edge14,OCT_CHBRK_CA.Vertex11]
  Reference2 = -> Assembly [OCT_CHBRK_AA.Edge20,OCT_CHBRK_AA.Vertex1]
FEATURE [App::FeaturePython] Joint003  label="Fixed"  # Assembly joint (typed FeaturePython)
  Activated = true
  AngleMax = 0
  AngleMin = 0
  Detach1 = false
  Detach2 = false
  Distance = 0
  Distance2 = 0
  EnableAngleMax = false
  EnableAngleMin = false
  EnableLengthMax = false
  EnableLengthMin = false
  JointType = 0 (Fixed)
  LengthMax = 0
  LengthMin = 0
  Offset2 = pos=(0,0,0) rot=(0,0,1;0.785398rad)
  Placement1 = pos=(35,14.4975,0) rot=(0,0,1;0rad)
  Placement2 = pos=(14.4975,35,0) rot=(0,0,1;0.785398rad)
  Reference1 = -> Assembly [OCT_CHBRK_CA.Edge17,OCT_CHBRK_CA.Vertex13]
  Reference2 = -> Assembly [OCT_CHBRK_AA001.Edge20,OCT_CHBRK_AA001.Vertex1]
FEATURE [App::FeaturePython] Joint004  label="Fixed"  # Assembly joint (typed FeaturePython)
  Activated = true
  AngleMax = 0
  AngleMin = 0
  Detach1 = false
  Detach2 = false
  Distance = 0
  Distance2 = 0
  EnableAngleMax = false
  EnableAngleMin = false
  EnableLengthMax = false
  EnableLengthMin = false
  JointType = 0 (Fixed)
  LengthMax = 0
  LengthMin = 0
  Placement1 = pos=(14.4975,35,0) rot=(0,0,1;0rad)
  Placement2 = pos=(14.4975,35,0) rot=(0,0,1;0rad)
  Reference1 = -> Assembly [OCT_CHBRK_AA002.Edge20,OCT_CHBRK_AA002.Vertex1]
  Reference2 = -> Assembly [OCT_CHBRK_CA.Edge20,OCT_CHBRK_CA.Vertex15]
FEATURE [App::FeaturePython] Joint005  label="Fixed"  # Assembly joint (typed FeaturePython)
  Activated = true
  AngleMax = 0
  AngleMin = 0
  Detach1 = false
  Detach2 = false
  Distance = 0
  Distance2 = 0
  EnableAngleMax = false
  EnableAngleMin = false
  EnableLengthMax = false
  EnableLengthMin = false
  JointType = 0 (Fixed)
  LengthMax = 0
  LengthMin = 0
  Offset2 = pos=(0,0,0) rot=(0,0,1;0.785398rad)
  Placement1 = pos=(14.4975,35,0) rot=(0,0,1;0rad)
  Placement2 = pos=(-14.4975,35,0) rot=(0,0,1;0.785398rad)
  Reference1 = -> Assembly [OCT_CHBRK_AA003.Edge20,OCT_CHBRK_AA003.Vertex1]
  Reference2 = -> Assembly [OCT_CHBRK_CA.Edge1,OCT_CHBRK_CA.Vertex1]
FEATURE [App::FeaturePython] Joint006  label="Fixed"  # Assembly joint (typed FeaturePython)
  Activated = true
  AngleMax = 0
  AngleMin = 0
  Detach1 = false
  Detach2 = false
  Distance = 0
  Distance2 = 0
  EnableAngleMax = false
  EnableAngleMin = false
  EnableLengthMax = false
  EnableLengthMin = false
  JointType = 0 (Fixed)
  LengthMax = 0
  LengthMin = 0
  Offset2 = pos=(0,0,0) rot=(0,0,1;1.5708rad)
  Placement1 = pos=(14.4975,35,0) rot=(0,0,1;0rad)
  Placement2 = pos=(-35,14.4975,0) rot=(0,0,1;1.5708rad)
  Reference1 = -> Assembly [OCT_CHBRK_AA004.Edge20,OCT_CHBRK_AA004.Vertex1]
  Reference2 = -> Assembly [OCT_CHBRK_CA.Edge2,OCT_CHBRK_CA.Vertex3]
FEATURE [App::FeaturePython] Joint007  label="Fixed"  # Assembly joint (typed FeaturePython)
  Activated = true
  AngleMax = 0
  AngleMin = 0
  Detach1 = false
  Detach2 = false
  Distance = 0
  Distance2 = 0
  EnableAngleMax = false
  EnableAngleMin = false
  EnableLengthMax = false
  EnableLengthMin = false
  JointType = 0 (Fixed)
  LengthMax = 0
  LengthMin = 0
  Offset2 = pos=(0,0,0) rot=(0,0,1;2.35619rad)
  Placement1 = pos=(14.4975,35,0) rot=(0,0,1;0rad)
  Placement2 = pos=(-35,-14.4975,0) rot=(0,0,1;2.35619rad)
  Reference1 = -> Assembly [OCT_CHBRK_AA005.Edge20,OCT_CHBRK_AA005.Vertex1]
  Reference2 = -> Assembly [OCT_CHBRK_CA.Edge5,OCT_CHBRK_CA.Vertex5]
FEATURE [Assembly::JointGroup] Joints
  Group = -> [GroundedJoint,Joint,Joint001,Joint002,Joint003,Joint004,Joint005,Joint006,Joint007]
FEATURE [Assembly::AssemblyObject] Assembly  label="OCT-CHMBR-A"
  Group = -> [Joints,OCT_CHBRK_CA,GroundedJoint,OCT_CHBRK_AA,OCT_CHBRK_AA001,OCT_CHBRK_AA002,OCT_CHBRK_AA003,OCT_CHBRK_AA004,OCT_CHBRK_AA005,OCT_CHBRK_BA,OCT_CHBRK_BA001,Joint,Joint001,Joint002,Joint003,Joint004,Joint005,Joint006,Joint007]
  Origin = -> Origin003
  Type = Assembly
